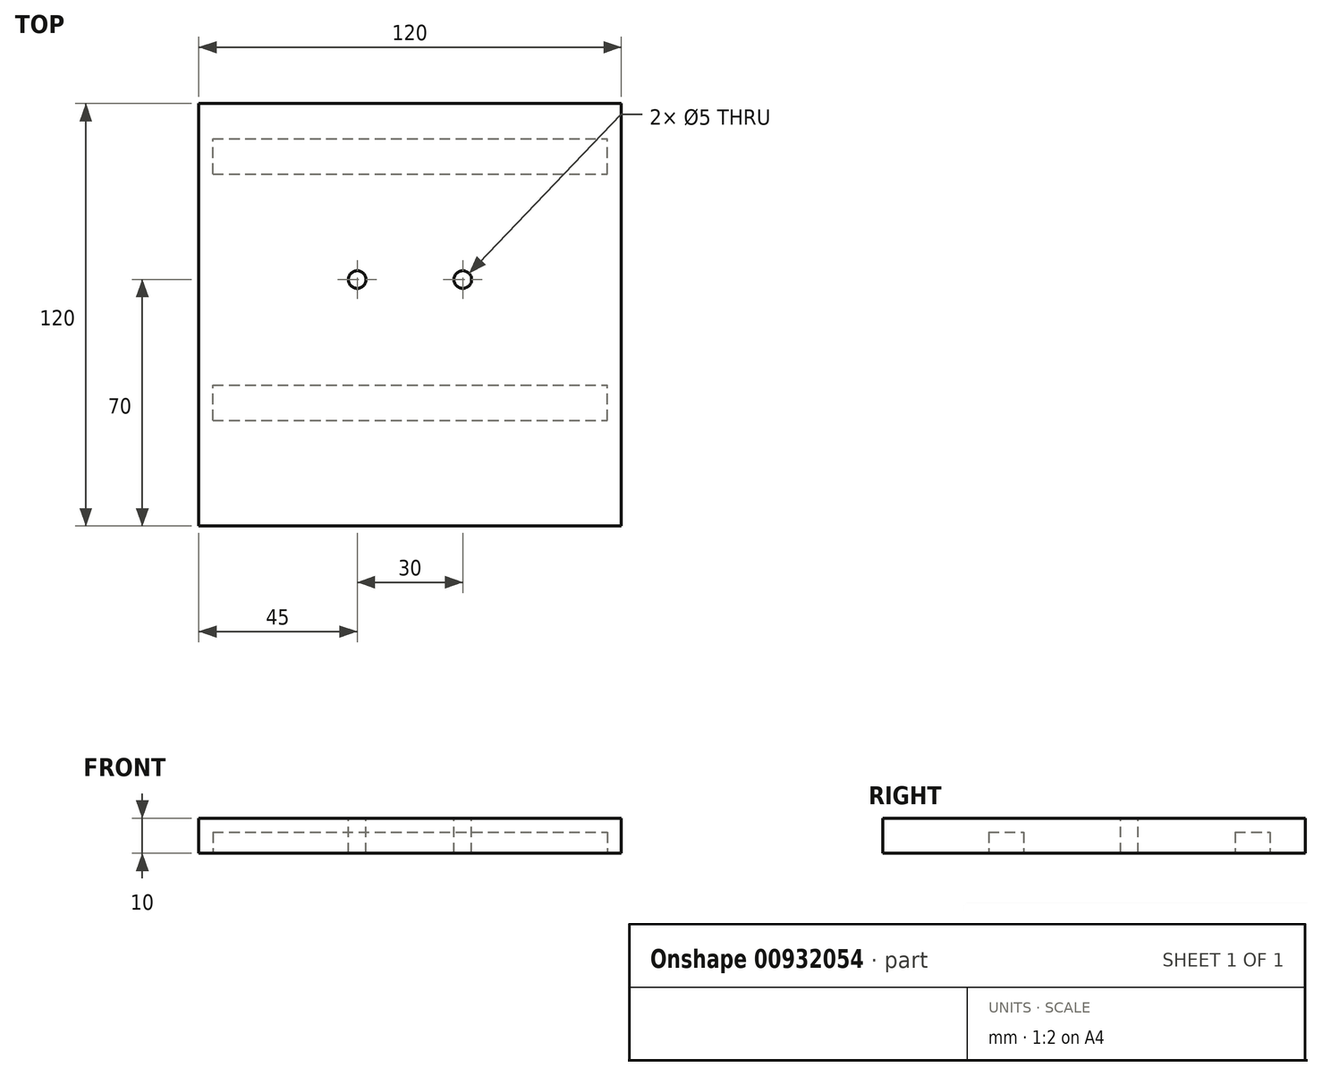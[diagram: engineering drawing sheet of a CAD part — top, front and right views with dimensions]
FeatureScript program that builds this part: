
annotation { "Feature Type Name" : "Feature", "Feature Type Description" : "" }
export const myFeature = defineFeature(function(context is Context, id is Id, definition is map)
    precondition{}
    {
        {
            var Q0;
            Q0=qCreatedBy(makeId("Top.planeOp"),FACE);
            var sketch = newSketch(context, id + "F0", { "sketchPlane" : qUnion([Q0])});
            skLineSegment(sketch, "E0.bottom", {"start": v(0, 0) * mm, "end": v(120, 0) * mm});
            skLineSegment(sketch, "E0.top", {"start": v(0, 120) * mm, "end": v(120, 120) * mm});
            skLineSegment(sketch, "E0.left", {"start": v(0, 0) * mm, "end": v(0, 120) * mm});
            skLineSegment(sketch, "E0.right", {"start": v(120, 0) * mm, "end": v(120, 120) * mm});
            skSolve(sketch);
        }
        {
            var Q0;
            Q0 = qSketchRegion(id + "F0", true);
            extrude(context, id + "F1", {"entities" : qUnion([Q0]), "depth" : 10 * mm, "offsetDistance" : 25 * mm});
        }
        {
            var Q0;
            Q0=makeQuery(id+"F1.opExtrude","CAP_FACE",FACE,{"disambiguationData":[OSD([sQuery(id+"F0.wireOp",EDGE,"E0.bottom"),sQuery(id+"F0.wireOp",EDGE,"E0.top"),sQuery(id+"F0.wireOp",EDGE,"E0.left"),sQuery(id+"F0.wireOp",EDGE,"E0.right")])],"isStart":true});
            var sketch = newSketch(context, id + "F2", { "sketchPlane" : qUnion([Q0])});
            skLineSegment(sketch, "E1.bottom", {"start": v(4, -40) * mm, "end": v(116, -40) * mm});
            skLineSegment(sketch, "E1.top", {"start": v(4, -30) * mm, "end": v(116, -30) * mm});
            skLineSegment(sketch, "E1.left", {"start": v(4, -30) * mm, "end": v(4, -40) * mm});
            skLineSegment(sketch, "E1.right", {"start": v(116, -30) * mm, "end": v(116, -40) * mm});
            skLineSegment(sketch, "E2.bottom", {"start": v(4, -100) * mm, "end": v(116, -100) * mm});
            skLineSegment(sketch, "E2.top", {"start": v(4, -110) * mm, "end": v(116, -110) * mm});
            skLineSegment(sketch, "E2.left", {"start": v(4, -100) * mm, "end": v(4, -110) * mm});
            skLineSegment(sketch, "E2.right", {"start": v(116, -100) * mm, "end": v(116, -110) * mm});
            skSolve(sketch);
        }
        {
            var Q0;
            Q0=makeQuery(id+"F2.imprint","IMPRINT",FACE,{"disambiguationData":[TD([[makeQuery(id+"F2.imprint","IMPRINT",EDGE,{"derivedFrom":sQuery(id+"F2.wireOp",EDGE,"E2.bottom")}),-1.0]])]});
            var Q1;
            Q1=makeQuery(id+"F2.imprint","IMPRINT",FACE,{"disambiguationData":[TD([[makeQuery(id+"F2.imprint","IMPRINT",EDGE,{"derivedFrom":sQuery(id+"F2.wireOp",EDGE,"E1.bottom")}),1.0]])]});
            extrude(context, id + "F3", {"entities" : qUnion([Q0, Q1]), "operationType" : NewBodyOperationType.REMOVE, "oppositeDirection" : true, "depth" : 6 * mm, "offsetDistance" : 25 * mm});
        }
        {
            var Q0;
            Q0=makeQuery(id+"F1.opExtrude","CAP_FACE",FACE,{"disambiguationData":[OSD([sQuery(id+"F0.wireOp",EDGE,"E0.bottom"),sQuery(id+"F0.wireOp",EDGE,"E0.top"),sQuery(id+"F0.wireOp",EDGE,"E0.left"),sQuery(id+"F0.wireOp",EDGE,"E0.right")])],"isStart":false});
            var sketch = newSketch(context, id + "F4", { "sketchPlane" : qUnion([Q0])});
            skPoint(sketch, "E3", {"position": v(45, 70) * mm});
            skPoint(sketch, "E4", {"position": v(75, 70) * mm});
            skSolve(sketch);
        }
        {
            var Q0;
            Q0=sQuery(id+"F4.wireOp",VERTEX,"E3");
            var Q1;
            Q1=sQuery(id+"F4.wireOp",VERTEX,"E4");
            var Q2;
            Q2=makeQuery(id+"F1.opExtrude","SWEPT_BODY",BODY,{"disambiguationData":[OSD([sQuery(id+"F0.wireOp",EDGE,"E0.bottom"),sQuery(id+"F0.wireOp",EDGE,"E0.top"),sQuery(id+"F0.wireOp",EDGE,"E0.left"),sQuery(id+"F0.wireOp",EDGE,"E0.right")])]});
            hole(context, id + "F5", {"style" : HoleStyle.SIMPLE, "endStyle" : HoleEndStyle.THROUGH, "holeDiameter" : 5 * mm, "majorDiameter" : 5 * mm, "isTappedThrough" : true, "tappedDepth" : 12 * mm, "tapClearance" : 3, "locations" : qUnion([Q0, Q1]), "scope" : qUnion([Q2])});
        }
    });
